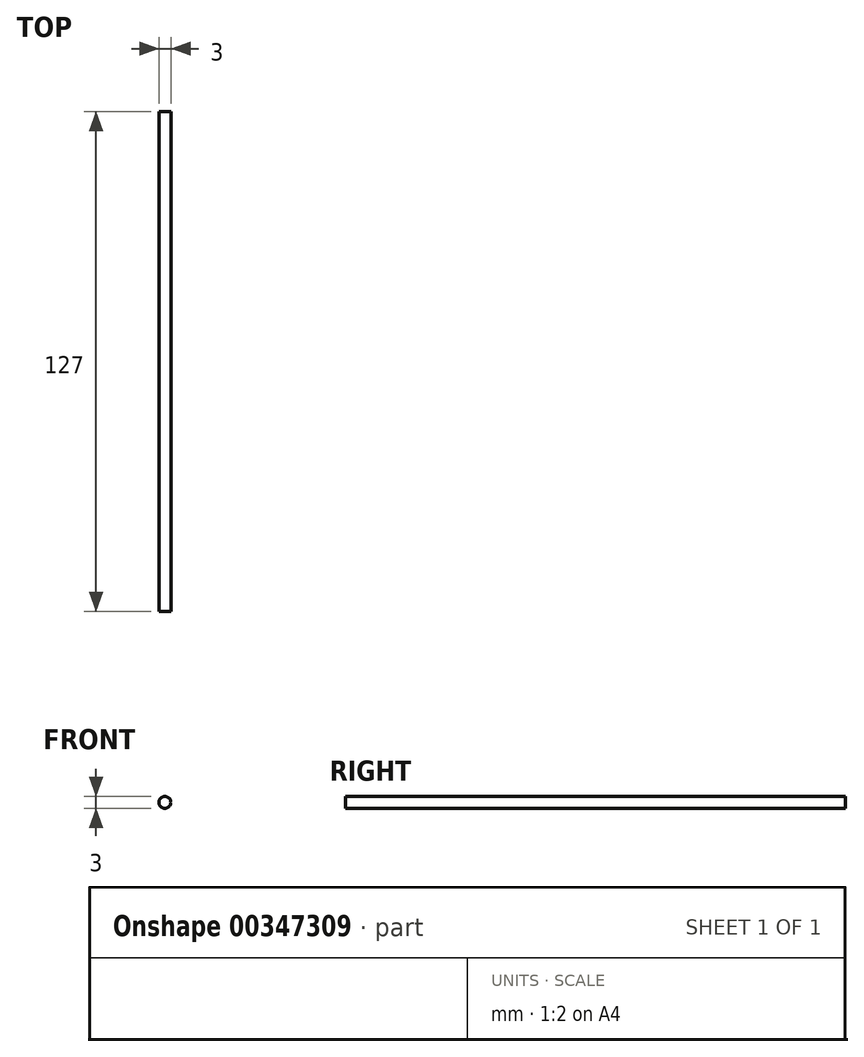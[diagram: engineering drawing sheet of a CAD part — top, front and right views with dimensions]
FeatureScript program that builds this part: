
annotation { "Feature Type Name" : "Feature", "Feature Type Description" : "" }
export const myFeature = defineFeature(function(context is Context, id is Id, definition is map)
    precondition{}
    {
        {
            var Q0;
            Q0=qCreatedBy(makeId("Front.planeOp"),FACE);
            var sketch = newSketch(context, id + "F0", { "sketchPlane" : qUnion([Q0])});
            skCircle(sketch, "E0", {"center": v(0, 0) * mm, "radius": 0.36 * mm});
            skCircle(sketch, "E1", {"center": v(0, -0.49) * mm, "radius": 1.5 * mm});
            skSolve(sketch);
        }
        {
            var Q0;
            Q0=makeQuery(id+"F0.imprint","IMPRINT",FACE,{"disambiguationData":[TD([[makeQuery(id+"F0.imprint","IMPRINT",EDGE,{"derivedFrom":sQuery(id+"F0.wireOp",EDGE,"E0")}),1.0]])]});
            var Q1;
            Q1=makeQuery(id+"F0.imprint","IMPRINT",FACE,{"disambiguationData":[TD([[makeQuery(id+"F0.imprint","IMPRINT",EDGE,{"derivedFrom":sQuery(id+"F0.wireOp",EDGE,"E0")}),-1.0]])]});
            extrude(context, id + "F1", {"entities" : qUnion([Q0, Q1]), "depth" : 127 * mm});
        }
    });
